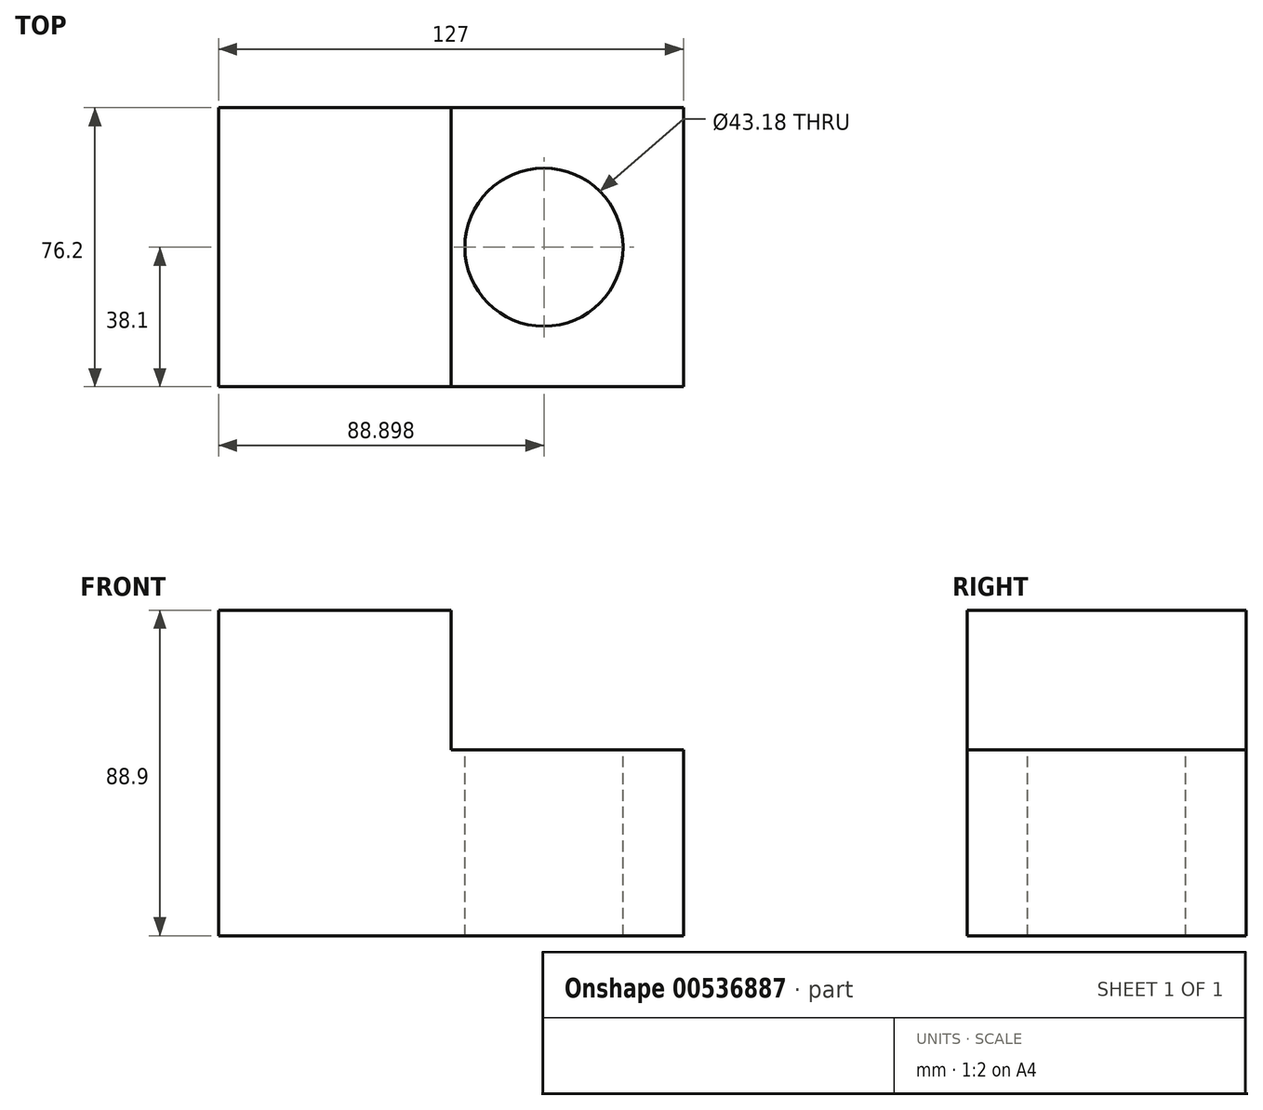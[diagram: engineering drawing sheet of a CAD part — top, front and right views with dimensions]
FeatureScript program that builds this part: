
annotation { "Feature Type Name" : "Feature", "Feature Type Description" : "" }
export const myFeature = defineFeature(function(context is Context, id is Id, definition is map)
    precondition{}
    {
        {
            var Q0;
            Q0=qCreatedBy(makeId("Front.planeOp"),FACE);
            var sketch = newSketch(context, id + "F0", { "sketchPlane" : qUnion([Q0])});
            skLineSegment(sketch, "E0.bottom", {"start": v(-40.32, 63.77) * mm, "end": v(23.18, 63.77) * mm});
            skLineSegment(sketch, "E0.top", {"start": v(-40.32, -25.13) * mm, "end": v(23.18, -25.13) * mm});
            skLineSegment(sketch, "E0.left", {"start": v(-40.32, 63.77) * mm, "end": v(-40.32, -25.13) * mm});
            skLineSegment(sketch, "E0.right", {"start": v(23.18, 63.77) * mm, "end": v(23.18, 25.67) * mm});
            skLineSegment(sketch, "E1", {"start": v(23.18, 25.67) * mm, "end": v(86.68, 25.67) * mm});
            skLineSegment(sketch, "E2", {"start": v(86.68, 25.67) * mm, "end": v(86.68, -25.13) * mm});
            skLineSegment(sketch, "E3", {"start": v(86.68, -25.13) * mm, "end": v(23.18, -25.13) * mm});
            skSolve(sketch);
        }
        {
            var Q0;
            Q0=makeQuery(id+"F0.imprint","IMPRINT",FACE,{"disambiguationData":[TD([[makeQuery(id+"F0.imprint","IMPRINT",EDGE,{"derivedFrom":sQuery(id+"F0.wireOp",EDGE,"E0.bottom")}),-1.0]])]});
            var Q1;
            Q1=sQuery(id+"F0.wireOp",EDGE,"E0.bottom");
            var Q2;
            Q2=sQuery(id+"F0.wireOp",EDGE,"E0.top");
            var Q3;
            Q3=sQuery(id+"F0.wireOp",EDGE,"E0.right");
            extrude(context, id + "F1", {"entities" : qUnion([Q0]), "surfaceEntities" : qUnion([Q1, Q2, Q3]), "depth" : 38.1 * mm, "offsetDistance" : 25.4 * mm, "hasSecondDirection" : true, "secondDirectionOppositeDirection" : true, "secondDirectionDepth" : 38.1 * mm});
        }
        {
            var Q0;
            Q0=makeQuery(id+"F1.opExtrude","SWEPT_FACE",FACE,{"disambiguationData":[OSD([sQuery(id+"F0.wireOp",EDGE,"E1")])]});
            var sketch = newSketch(context, id + "F2", { "sketchPlane" : qUnion([Q0])});
            skCircle(sketch, "E4", {"center": v(48.58, 0) * mm, "radius": 21.59 * mm});
            skSolve(sketch);
        }
        {
            var Q0;
            Q0 = qSketchRegion(id + "F2", true);
            extrude(context, id + "F3", {"entities" : qUnion([Q0]), "operationType" : NewBodyOperationType.REMOVE, "endBound" : BoundingType.UP_TO_NEXT, "oppositeDirection" : true, "depth" : 25.4 * mm, "offsetDistance" : 25.4 * mm});
        }
    });
